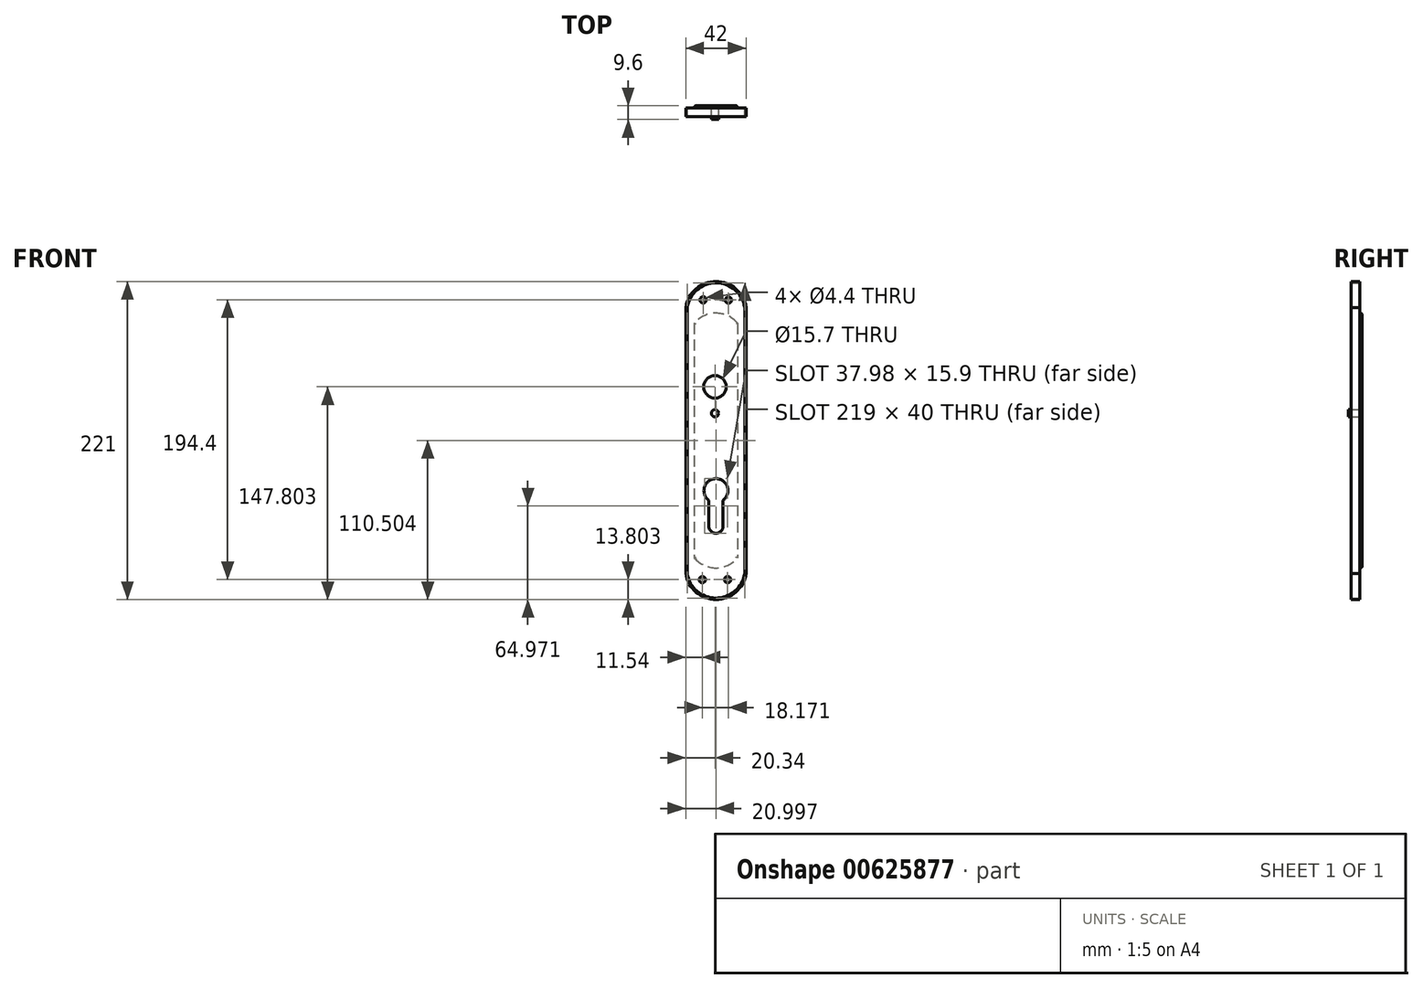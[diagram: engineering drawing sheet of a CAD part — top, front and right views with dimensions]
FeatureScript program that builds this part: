
annotation { "Feature Type Name" : "Feature", "Feature Type Description" : "" }
export const myFeature = defineFeature(function(context is Context, id is Id, definition is map)
    precondition{}
    {
        {
            var Q0;
            Q0=qCreatedBy(makeId("Front.planeOp"),FACE);
            var sketch = newSketch(context, id + "F0", { "sketchPlane" : qUnion([Q0])});
            skLineSegment(sketch, "E0", {"start": v(-19.34, 91.37) * mm, "end": v(-19.34, -93.63) * mm});
            skLineSegment(sketch, "E1", {"start": v(20.66, 91.37) * mm, "end": v(20.66, -93.63) * mm});
            skCircle(sketch, "E2", {"center": v(-8.23, 96.57) * mm, "radius": 2.2 * mm});
            skCircle(sketch, "E3.MirrorC", {"center": v(9.37, 96.47) * mm, "radius": 2.2 * mm});
            skCircle(sketch, "E4.MirrorC", {"center": v(-8.8, -97.83) * mm, "radius": 2.2 * mm});
            skCircle(sketch, "E5.MirrorC", {"center": v(8.8, -97.83) * mm, "radius": 2.2 * mm});
            skArc(sketch, "E6", {"start": v(-19.34, -93.63) * mm, "mid": v(0.66, -110.63) * mm, "end": v(20.66, -93.63) * mm});
            skArc(sketch, "E7", {"start": v(20.66, 91.37) * mm, "mid": v(0.66, 108.37) * mm, "end": v(-19.34, 91.37) * mm});
            skLineSegment(sketch, "E8", {"start": v(21.66, 91.37) * mm, "end": v(21.66, -93.63) * mm});
            skArc(sketch, "E9", {"start": v(-20.34, -93.63) * mm, "mid": v(0.66, -111.63) * mm, "end": v(21.66, -93.63) * mm});
            skLineSegment(sketch, "E10", {"start": v(-20.34, -93.63) * mm, "end": v(-20.34, 91.37) * mm});
            skArc(sketch, "E11", {"start": v(21.66, 91.37) * mm, "mid": v(0.66, 109.37) * mm, "end": v(-20.34, 91.37) * mm});
            skSolve(sketch);
        }
        {
            var Q0;
            Q0=makeQuery(id+"F0.imprint","IMPRINT",FACE,{"disambiguationData":[TD([[makeQuery(id+"F0.imprint","IMPRINT",EDGE,{"derivedFrom":sQuery(id+"F0.wireOp",EDGE,"E0")}),-1.0]])]});
            extrude(context, id + "F1", {"entities" : qUnion([Q0]), "depth" : 6 * mm, "offsetDistance" : 25 * mm});
        }
        {
            var Q0;
            Q0=makeQuery(id+"F0.imprint","IMPRINT",FACE,{"disambiguationData":[TD([[makeQuery(id+"F0.imprint","IMPRINT",EDGE,{"derivedFrom":sQuery(id+"F0.wireOp",EDGE,"E0")}),1.0]])]});
            extrude(context, id + "F2", {"entities" : qUnion([Q0]), "operationType" : NewBodyOperationType.ADD, "oppositeDirection" : true, "depth" : 0.1 * mm, "offsetDistance" : 25 * mm});
        }
        {
            var Q0;
            Q0=makeQuery(id+"F2.opExtrude","CAP_FACE",FACE,{"disambiguationData":[OSD([sQuery(id+"F0.wireOp",EDGE,"E0"),sQuery(id+"F0.wireOp",EDGE,"E1"),sQuery(id+"F0.wireOp",EDGE,"E2"),sQuery(id+"F0.wireOp",EDGE,"E3.MirrorC"),sQuery(id+"F0.wireOp",EDGE,"E4.MirrorC"),sQuery(id+"F0.wireOp",EDGE,"E5.MirrorC"),sQuery(id+"F0.wireOp",EDGE,"E6"),sQuery(id+"F0.wireOp",EDGE,"E7")])],"isStart":false});
            var sketch = newSketch(context, id + "F3", { "sketchPlane" : qUnion([Q0])});
            skLineSegment(sketch, "E12", {"start": v(-15.66, 80.35) * mm, "end": v(-15.66, -82.65) * mm});
            skLineSegment(sketch, "E13", {"start": v(14.34, 80.35) * mm, "end": v(14.34, -82.65) * mm});
            skArc(sketch, "E14", {"start": v(14.34, 80.35) * mm, "mid": v(-0.66, 87.35) * mm, "end": v(-15.66, 80.35) * mm});
            skArc(sketch, "E15", {"start": v(-15.66, -82.65) * mm, "mid": v(-0.66, -89.65) * mm, "end": v(14.34, -82.65) * mm});
            skSolve(sketch);
        }
        {
            var Q0;
            Q0=makeQuery(id+"F3.imprint","IMPRINT",FACE,{"disambiguationData":[TD([[makeQuery(id+"F3.imprint","IMPRINT",EDGE,{"derivedFrom":sQuery(id+"F3.wireOp",EDGE,"E12")}),1.0]])]});
            extrude(context, id + "F4", {"entities" : qUnion([Q0]), "operationType" : NewBodyOperationType.ADD, "depth" : 1.5 * mm, "offsetDistance" : 25 * mm});
        }
        {
            var Q0;
            Q0=makeQuery(id+"F4.opExtrude","CAP_EDGE",EDGE,{"disambiguationData":[OSD([sQuery(id+"F3.wireOp",EDGE,"E12")])],"isStart":false});
            var Q1;
            Q1=makeQuery(id+"F4.opExtrude","CAP_EDGE",EDGE,{"disambiguationData":[OSD([sQuery(id+"F3.wireOp",EDGE,"E15")])],"isStart":false});
            var Q2;
            Q2=makeQuery(id+"F4.opExtrude","CAP_EDGE",EDGE,{"disambiguationData":[OSD([sQuery(id+"F3.wireOp",EDGE,"E14")])],"isStart":false});
            var Q3;
            Q3=makeQuery(id+"F4.opExtrude","CAP_EDGE",EDGE,{"disambiguationData":[OSD([sQuery(id+"F3.wireOp",EDGE,"E13")])],"isStart":false});
            fillet(context, id + "F5", {"entities" : qUnion([Q0, Q1, Q2, Q3]), "radius" : 1 * mm, "allowEdgeOverflow" : false});
        }
        {
            var Q0;
            Q0=makeQuery(id+"F4.opExtrude","CAP_FACE",FACE,{"disambiguationData":[OSD([sQuery(id+"F3.wireOp",EDGE,"E12"),sQuery(id+"F3.wireOp",EDGE,"E13"),sQuery(id+"F3.wireOp",EDGE,"E14"),sQuery(id+"F3.wireOp",EDGE,"E15")])],"isStart":false});
            var sketch = newSketch(context, id + "F6", { "sketchPlane" : qUnion([Q0])});
            skCircle(sketch, "E16", {"center": v(0, 36.17) * mm, "radius": 7.85 * mm});
            skLineSegment(sketch, "E17", {"start": v(4.34, -60.65) * mm, "end": v(4.34, -42.65) * mm});
            skLineSegment(sketch, "E18", {"start": v(-5.66, -42.65) * mm, "end": v(-5.66, -60.65) * mm});
            skArc(sketch, "E19", {"start": v(-5.66, -60.65) * mm, "mid": v(-0.66, -65.65) * mm, "end": v(4.34, -60.65) * mm});
            skArc(sketch, "E20", {"start": v(4.34, -42.65) * mm, "mid": v(-0.66, -27.67) * mm, "end": v(-5.66, -42.65) * mm});
            skSolve(sketch);
        }
        {
            var Q0;
            Q0=makeQuery(id+"F6.imprint","IMPRINT",FACE,{"disambiguationData":[TD([[makeQuery(id+"F6.imprint","IMPRINT",EDGE,{"derivedFrom":sQuery(id+"F6.wireOp",EDGE,"E17")}),1.0]])]});
            var Q1;
            Q1=makeQuery(id+"F6.imprint","IMPRINT",FACE,{"disambiguationData":[TD([[makeQuery(id+"F6.imprint","IMPRINT",EDGE,{"derivedFrom":sQuery(id+"F6.wireOp",EDGE,"E16")}),1.0]])]});
            extrude(context, id + "F7", {"entities" : qUnion([Q0, Q1]), "operationType" : NewBodyOperationType.REMOVE, "oppositeDirection" : true, "depth" : 25 * mm, "offsetDistance" : 25 * mm});
        }
        {
            var Q0;
            Q0=makeQuery(id+"F0.imprint","IMPRINT",FACE,{"disambiguationData":[TD([[makeQuery(id+"F0.imprint","IMPRINT",EDGE,{"derivedFrom":sQuery(id+"F0.wireOp",EDGE,"E0")}),1.0]])]});
            var sketch = newSketch(context, id + "F8", { "sketchPlane" : qUnion([Q0])});
            skLineSegment(sketch, "E21", {"start": v(0, 49.57) * mm, "end": v(0, 0) * mm, "construction": true});
            skCircle(sketch, "E22", {"center": v(0, 17.82) * mm, "radius": 2.5 * mm});
            skSolve(sketch);
        }
        {
            var Q0;
            Q0=makeQuery(id+"F8.imprint","IMPRINT",FACE,{"disambiguationData":[TD([[makeQuery(id+"F8.imprint","IMPRINT",EDGE,{"derivedFrom":sQuery(id+"F8.wireOp",EDGE,"E22")}),1.0]])]});
            extrude(context, id + "F9", {"entities" : qUnion([Q0]), "operationType" : NewBodyOperationType.ADD, "depth" : 8 * mm, "offsetDistance" : 25 * mm});
        }
    });
